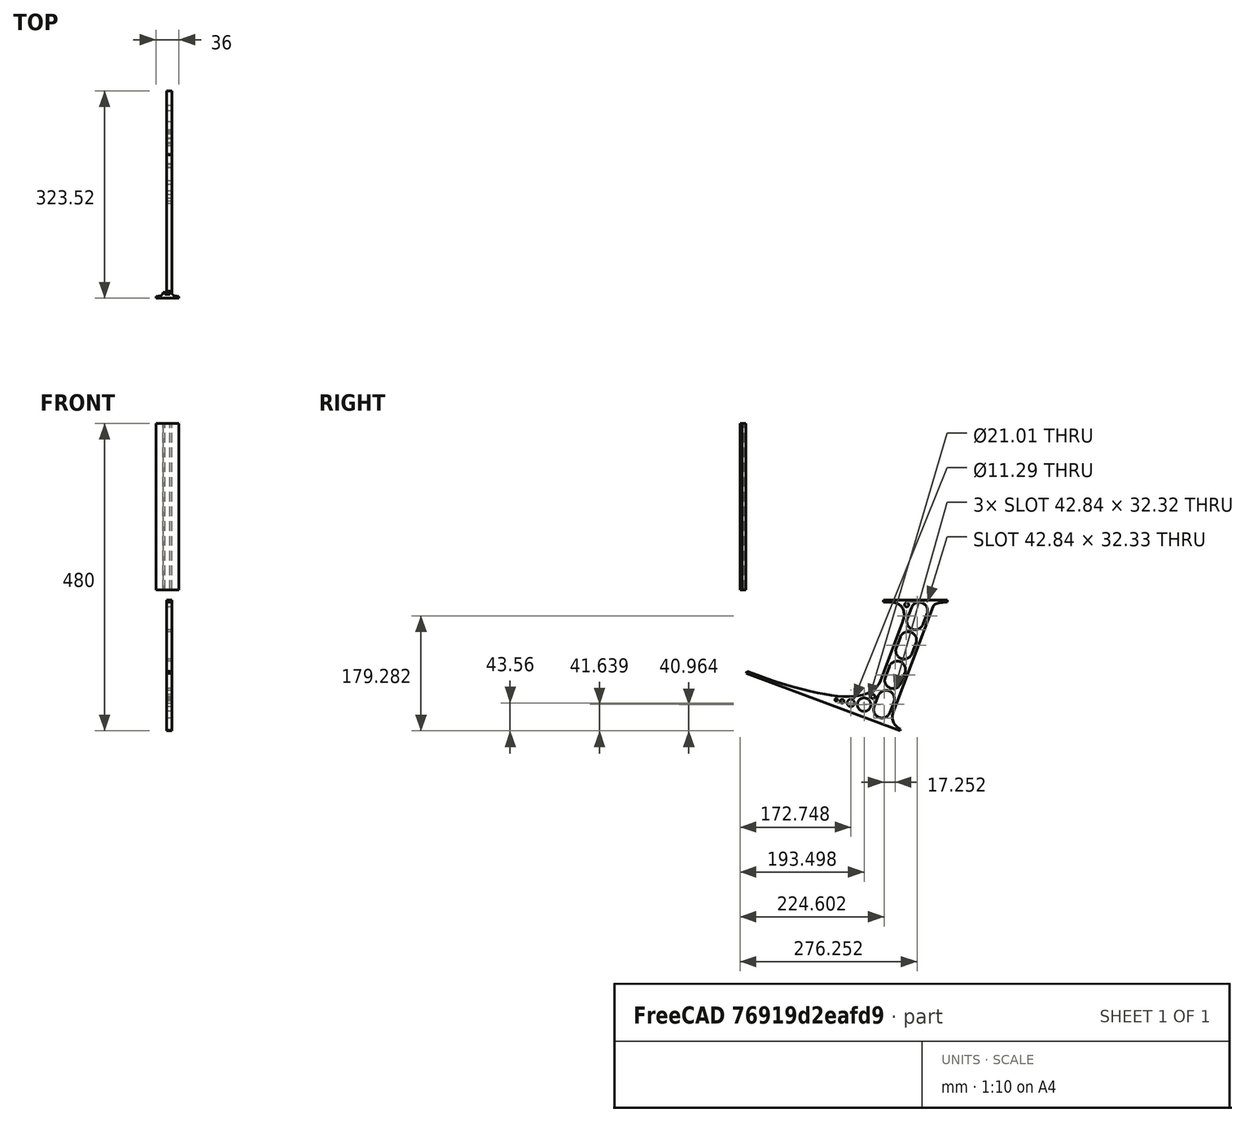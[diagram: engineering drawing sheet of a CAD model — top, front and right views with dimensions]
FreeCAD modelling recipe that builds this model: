
FCSTD DOCUMENT  (FreeCAD 0.19R0.19.2)
Label: laptopStand087
License: All rights reserved
LicenseURL: http://en.wikipedia.org/wiki/All_rights_reserved
objects: Sketcher::SketchObject×3, Part::Extrusion×3
note: 6 computed .brp shape members not serialized (recipe doc carries the construction recipe); baked Part::Feature solids carry a one-line shape summary decoded from their .brp

FEATURE [Sketcher::SketchObject] Sketch
  FullyConstrained = false
  sketch-geometry (236):
    g0: LineSegment StartX=-10.9272 StartY=-82.7794 StartZ=0 EndX=46.0728 EndY=-51.4823 EndZ=0
    g1: LineSegment StartX=366.073 StartY=-91.7794 StartZ=0 EndX=318.073 EndY=-65.424 EndZ=0
    g2: LineSegment StartX=-10.9272 StartY=77.3346 StartZ=0 EndX=-10.9272 EndY=-82.7794 EndZ=0
    g3: LineSegment StartX=375.073 StartY=-82.7794 StartZ=0 EndX=375.073 EndY=83.9235 EndZ=0
    g4: LineSegment StartX=-1.92719 StartY=-91.7794 StartZ=0 EndX=46.0728 EndY=-91.7794 EndZ=0
    g5: LineSegment StartX=318.073 StartY=124.221 StartZ=0 EndX=366.073 EndY=124.221 EndZ=0
    g6: LineSegment StartX=306.073 StartY=77.3346 StartZ=0 EndX=306.073 EndY=-44.8935 EndZ=0
    g7: LineSegment StartX=318.073 StartY=83.9235 StartZ=0 EndX=318.073 EndY=-51.4823 EndZ=0
    g8: LineSegment StartX=318.073 StartY=-51.4823 StartZ=0 EndX=375.073 EndY=-82.7794 EndZ=0
    g9: LineSegment StartX=318.073 StartY=-65.424 StartZ=0 EndX=318.073 EndY=-91.7794 EndZ=0
    g10: LineSegment StartX=318.073 StartY=-91.7794 StartZ=0 EndX=366.073 EndY=-91.7794 EndZ=0
    g11: LineSegment StartX=58.0728 StartY=-44.8935 StartZ=0 EndX=58.0728 EndY=77.3346 EndZ=0
    g12: LineSegment StartX=46.0728 StartY=-65.424 StartZ=0 EndX=-1.92719 EndY=-91.7794 EndZ=0
    g13: LineSegment StartX=46.0728 StartY=-65.424 StartZ=0 EndX=46.0728 EndY=-91.7794 EndZ=0
    g14: LineSegment StartX=46.0728 StartY=77.3346 StartZ=0 EndX=46.0728 EndY=-51.4823 EndZ=0
    g15: LineSegment StartX=-42.9272 StartY=136.221 StartZ=0 EndX=-42.9272 EndY=-103.779 EndZ=0
    g16: LineSegment StartX=407.073 StartY=136.221 StartZ=0 EndX=407.073 EndY=-103.779 EndZ=0
    g17: ArcOfCircle CenterX=-26.9272 CenterY=22.1087 CenterZ=0 NormalX=0 NormalY=0 NormalZ=1 AngleXU=0 Radius=8 StartAngle=1e-16 EndAngle=3.14159
    g18: ArcOfCircle CenterX=-26.9272 CenterY=-83.7794 CenterZ=0 NormalX=0 NormalY=0 NormalZ=1 AngleXU=0 Radius=8 StartAngle=3.14159 EndAngle=6.28319
    g19: LineSegment StartX=-34.9272 StartY=22.1087 StartZ=0 EndX=-34.9272 EndY=-83.7794 EndZ=0
    g20: LineSegment StartX=-18.9272 StartY=22.1087 StartZ=0 EndX=-18.9272 EndY=-83.7794 EndZ=0
    g21: ArcOfCircle CenterX=391.073 CenterY=22.1087 CenterZ=0 NormalX=0 NormalY=0 NormalZ=1 AngleXU=0 Radius=8 StartAngle=-4.4e-15 EndAngle=3.14159
    g22: LineSegment StartX=399.073 StartY=22.1087 StartZ=0 EndX=399.073 EndY=-83.7794 EndZ=0
    g23: LineSegment StartX=383.073 StartY=22.1087 StartZ=0 EndX=383.073 EndY=-83.7794 EndZ=0
    g24: ArcOfCircle CenterX=391.073 CenterY=-83.7794 CenterZ=0 NormalX=0 NormalY=0 NormalZ=1 AngleXU=0 Radius=8 StartAngle=3.14159 EndAngle=6.28319
    g25: Circle CenterX=175.022 CenterY=27.0628 CenterZ=0 NormalX=0 NormalY=0 NormalZ=1 AngleXU=0 Radius=1
    g26: Circle CenterX=179.022 CenterY=24.8665 CenterZ=0 NormalX=0 NormalY=0 NormalZ=1 AngleXU=0 Radius=1
    g27: Circle CenterX=179.022 CenterY=27.0628 CenterZ=0 NormalX=0 NormalY=0 NormalZ=1 AngleXU=0 Radius=1
    g28: BSplineCurve PolesCount=3 KnotsCount=2 Degree=2 IsPeriodic=0
    g29: GeomPoint X=175.022 Y=27.0628 Z=0
    g30: GeomPoint X=179.022 Y=27.0628 Z=0
    g31: Circle CenterX=189.124 CenterY=27.0628 CenterZ=0 NormalX=0 NormalY=0 NormalZ=1 AngleXU=0 Radius=1
    g32: Circle CenterX=185.124 CenterY=24.8665 CenterZ=0 NormalX=0 NormalY=0 NormalZ=1 AngleXU=0 Radius=1
    g33: Circle CenterX=185.124 CenterY=27.0628 CenterZ=0 NormalX=0 NormalY=0 NormalZ=1 AngleXU=0 Radius=1
    g34: BSplineCurve PolesCount=3 KnotsCount=2 Degree=2 IsPeriodic=0
    g35: GeomPoint X=189.124 Y=27.0628 Z=0
    g36: GeomPoint X=185.124 Y=27.0628 Z=0
    g37: Circle CenterX=175.022 CenterY=5.37834 CenterZ=0 NormalX=0 NormalY=0 NormalZ=1 AngleXU=0 Radius=1
    g38: Circle CenterX=179.022 CenterY=7.57463 CenterZ=0 NormalX=0 NormalY=0 NormalZ=1 AngleXU=0 Radius=1
    g39: Circle CenterX=179.022 CenterY=5.34704 CenterZ=0 NormalX=0 NormalY=0 NormalZ=1 AngleXU=0 Radius=1
    g40: BSplineCurve PolesCount=3 KnotsCount=2 Degree=2 IsPeriodic=0
    g41: GeomPoint X=175.022 Y=5.37834 Z=0
    g42: GeomPoint X=179.022 Y=5.34704 Z=0
    g43: Circle CenterX=189.124 CenterY=5.37834 CenterZ=0 NormalX=0 NormalY=0 NormalZ=1 AngleXU=0 Radius=1
    g44: Circle CenterX=185.124 CenterY=7.57463 CenterZ=0 NormalX=0 NormalY=0 NormalZ=1 AngleXU=0 Radius=1
    g45: Circle CenterX=185.124 CenterY=5.34704 CenterZ=0 NormalX=0 NormalY=0 NormalZ=1 AngleXU=0 Radius=1
    g46: BSplineCurve PolesCount=3 KnotsCount=2 Degree=2 IsPeriodic=0
    g47: GeomPoint X=189.124 Y=5.37834 Z=0
    g48: GeomPoint X=185.124 Y=5.34704 Z=0
    g49: Circle CenterX=165.871 CenterY=18.1458 CenterZ=0 NormalX=0 NormalY=0 NormalZ=1 AngleXU=0 Radius=1
    g50: Circle CenterX=169.377 CenterY=16.2206 CenterZ=0 NormalX=0 NormalY=0 NormalZ=1 AngleXU=0 Radius=1
    g51: Circle CenterX=165.871 CenterY=14.2954 CenterZ=0 NormalX=0 NormalY=0 NormalZ=1 AngleXU=0 Radius=1
    g52: BSplineCurve PolesCount=3 KnotsCount=2 Degree=2 IsPeriodic=0
    g53: GeomPoint X=165.871 Y=18.1458 Z=0
    g54: GeomPoint X=165.871 Y=14.2954 Z=0
    g55: Circle CenterX=198.275 CenterY=18.1458 CenterZ=0 NormalX=0 NormalY=0 NormalZ=1 AngleXU=0 Radius=1
    g56: Circle CenterX=194.768 CenterY=16.2206 CenterZ=0 NormalX=0 NormalY=0 NormalZ=1 AngleXU=0 Radius=1
    g57: Circle CenterX=198.275 CenterY=14.2954 CenterZ=0 NormalX=0 NormalY=0 NormalZ=1 AngleXU=0 Radius=1
    g58: BSplineCurve PolesCount=3 KnotsCount=2 Degree=2 IsPeriodic=0
    g59: GeomPoint X=198.275 Y=18.1458 Z=0
    g60: GeomPoint X=198.275 Y=14.2954 Z=0
    g61: LineSegment StartX=165.871 StartY=18.1458 StartZ=0 EndX=58.0728 EndY=77.3346 EndZ=0
    g62: LineSegment StartX=58.0728 StartY=-44.8935 StartZ=0 EndX=165.871 EndY=14.2954 EndZ=0
    g63: LineSegment StartX=198.275 StartY=18.1458 StartZ=0 EndX=306.073 EndY=77.3346 EndZ=0
    g64: LineSegment StartX=198.275 StartY=14.2954 StartZ=0 EndX=306.073 EndY=-44.8935 EndZ=0
    g65: LineSegment StartX=407.073 StartY=-103.779 StartZ=0 EndX=-42.9272 EndY=-103.779 EndZ=0
    g66: LineSegment StartX=407.073 StartY=136.221 StartZ=0 EndX=-42.9272 EndY=136.221 EndZ=0
    g67: LineSegment StartX=46.0728 StartY=77.3346 StartZ=0 EndX=-10.9272 EndY=77.3346 EndZ=0
    g68: LineSegment StartX=46.0728 StartY=105.865 StartZ=0 EndX=31.5028 EndY=105.865 EndZ=0
    g69: LineSegment StartX=46.0728 StartY=124.221 StartZ=0 EndX=46.0728 EndY=105.865 EndZ=0
    g70: LineSegment StartX=-1.92719 StartY=124.221 StartZ=0 EndX=31.5028 EndY=105.865 EndZ=0
    g71: LineSegment StartX=46.0728 StartY=124.221 StartZ=0 EndX=-1.92719 EndY=124.221 EndZ=0
    g72: LineSegment StartX=318.073 StartY=83.9235 StartZ=0 EndX=375.073 EndY=83.9235 EndZ=0
    g73: LineSegment StartX=318.073 StartY=105.865 StartZ=0 EndX=332.643 EndY=105.865 EndZ=0
    g74: LineSegment StartX=332.643 StartY=105.865 StartZ=0 EndX=366.073 EndY=124.221 EndZ=0
    g75: LineSegment StartX=318.073 StartY=124.221 StartZ=0 EndX=318.073 EndY=105.865 EndZ=0
    g76: Circle CenterX=125.607 CenterY=54.1951 CenterZ=0 NormalX=0 NormalY=0 NormalZ=1 AngleXU=0 Radius=1
    g77: Circle CenterX=139.632 CenterY=46.4944 CenterZ=0 NormalX=0 NormalY=0 NormalZ=1 AngleXU=0 Radius=1
    g78: Circle CenterX=127.326 CenterY=56.7187 CenterZ=0 NormalX=0 NormalY=0 NormalZ=1 AngleXU=0 Radius=1
    g79: BSplineCurve PolesCount=3 KnotsCount=2 Degree=2 IsPeriodic=0
    g80: GeomPoint X=125.607 Y=54.1951 Z=0
    g81: GeomPoint X=127.326 Y=56.7187 Z=0
    g82: Circle CenterX=236.821 CenterY=56.7187 CenterZ=0 NormalX=0 NormalY=0 NormalZ=1 AngleXU=0 Radius=1
    g83: Circle CenterX=224.513 CenterY=46.4944 CenterZ=0 NormalX=0 NormalY=0 NormalZ=1 AngleXU=0 Radius=1
    g84: Circle CenterX=238.538 CenterY=54.1951 CenterZ=0 NormalX=0 NormalY=0 NormalZ=1 AngleXU=0 Radius=1
    g85: BSplineCurve PolesCount=3 KnotsCount=2 Degree=2 IsPeriodic=0
    g86: GeomPoint X=236.821 Y=56.7187 Z=0
    g87: GeomPoint X=238.538 Y=54.1951 Z=0
    g88: Circle CenterX=238.538 CenterY=-21.7539 CenterZ=0 NormalX=0 NormalY=0 NormalZ=1 AngleXU=0 Radius=1
    g89: Circle CenterX=224.513 CenterY=-14.0532 CenterZ=0 NormalX=0 NormalY=0 NormalZ=1 AngleXU=0 Radius=1
    g90: Circle CenterX=236.821 CenterY=-24.2775 CenterZ=0 NormalX=0 NormalY=0 NormalZ=1 AngleXU=0 Radius=1
    g91: BSplineCurve PolesCount=3 KnotsCount=2 Degree=2 IsPeriodic=0
    g92: GeomPoint X=238.538 Y=-21.7539 Z=0
    g93: GeomPoint X=236.821 Y=-24.2775 Z=0
    g94: Circle CenterX=125.607 CenterY=-21.7539 CenterZ=0 NormalX=0 NormalY=0 NormalZ=1 AngleXU=0 Radius=1
    g95: Circle CenterX=139.632 CenterY=-14.0532 CenterZ=0 NormalX=0 NormalY=0 NormalZ=1 AngleXU=0 Radius=1
    g96: Circle CenterX=127.325 CenterY=-24.2775 CenterZ=0 NormalX=0 NormalY=0 NormalZ=1 AngleXU=0 Radius=1
    g97: BSplineCurve PolesCount=3 KnotsCount=2 Degree=2 IsPeriodic=0
    g98: GeomPoint X=125.607 Y=-21.7539 Z=0
    g99: GeomPoint X=127.325 Y=-24.2775 Z=0
    g100: Circle CenterX=302.996 CenterY=111.695 CenterZ=0 NormalX=0 NormalY=0 NormalZ=1 AngleXU=0 Radius=1
    g101: Circle CenterX=306.073 CenterY=114.251 CenterZ=0 NormalX=0 NormalY=0 NormalZ=1 AngleXU=0 Radius=1
    g102: Circle CenterX=306.073 CenterY=110.251 CenterZ=0 NormalX=0 NormalY=0 NormalZ=1 AngleXU=0 Radius=1
    g103: BSplineCurve PolesCount=3 KnotsCount=2 Degree=2 IsPeriodic=0
    g104: GeomPoint X=302.996 Y=111.695 Z=0
    g105: GeomPoint X=306.073 Y=110.251 Z=0
    g106: Circle CenterX=306.073 CenterY=95.2763 CenterZ=0 NormalX=0 NormalY=0 NormalZ=1 AngleXU=0 Radius=1
    g107: Circle CenterX=306.073 CenterY=91.2763 CenterZ=0 NormalX=0 NormalY=0 NormalZ=1 AngleXU=0 Radius=1
    g108: Circle CenterX=302.567 CenterY=89.3511 CenterZ=0 NormalX=0 NormalY=0 NormalZ=1 AngleXU=0 Radius=1
    g109: BSplineCurve PolesCount=3 KnotsCount=2 Degree=2 IsPeriodic=0
    g110: GeomPoint X=306.073 Y=95.2763 Z=0
    g111: GeomPoint X=302.567 Y=89.3511 Z=0
    g112: LineSegment StartX=306.073 StartY=110.251 StartZ=0 EndX=306.073 EndY=95.2763 EndZ=0
    g113: LineSegment StartX=302.996 StartY=111.695 StartZ=0 EndX=236.821 EndY=56.7187 EndZ=0
    g114: LineSegment StartX=238.538 StartY=54.1951 StartZ=0 EndX=302.567 EndY=89.3511 EndZ=0
    g115: Circle CenterX=61.1496 CenterY=111.695 CenterZ=0 NormalX=0 NormalY=0 NormalZ=1 AngleXU=0 Radius=1
    g116: Circle CenterX=58.0728 CenterY=114.251 CenterZ=0 NormalX=0 NormalY=0 NormalZ=1 AngleXU=0 Radius=1
    g117: Circle CenterX=58.0728 CenterY=110.251 CenterZ=0 NormalX=0 NormalY=0 NormalZ=1 AngleXU=0 Radius=1
    g118: BSplineCurve PolesCount=3 KnotsCount=2 Degree=2 IsPeriodic=0
    g119: GeomPoint X=61.1496 Y=111.695 Z=0
    g120: GeomPoint X=58.0728 Y=110.251 Z=0
    g121: Circle CenterX=61.5791 CenterY=89.3511 CenterZ=0 NormalX=0 NormalY=0 NormalZ=1 AngleXU=0 Radius=1
    g122: Circle CenterX=58.0728 CenterY=91.2763 CenterZ=0 NormalX=0 NormalY=0 NormalZ=1 AngleXU=0 Radius=1
    g123: Circle CenterX=58.0728 CenterY=95.2763 CenterZ=0 NormalX=0 NormalY=0 NormalZ=1 AngleXU=0 Radius=1
    g124: BSplineCurve PolesCount=3 KnotsCount=2 Degree=2 IsPeriodic=0
    g125: GeomPoint X=61.5791 Y=89.3511 Z=0
    g126: GeomPoint X=58.0728 Y=95.2763 Z=0
    g127: LineSegment StartX=58.0728 StartY=110.251 StartZ=0 EndX=58.0728 EndY=95.2763 EndZ=0
    g128: LineSegment StartX=61.1496 StartY=111.695 StartZ=0 EndX=127.326 EndY=56.7187 EndZ=0
    g129: LineSegment StartX=125.607 StartY=54.1951 StartZ=0 EndX=61.5791 EndY=89.3511 EndZ=0
    g130: Circle CenterX=61.5791 CenterY=-56.9099 CenterZ=0 NormalX=0 NormalY=0 NormalZ=1 AngleXU=0 Radius=1
    g131: Circle CenterX=58.0728 CenterY=-58.8351 CenterZ=0 NormalX=0 NormalY=0 NormalZ=1 AngleXU=0 Radius=1
    g132: Circle CenterX=58.0728 CenterY=-62.8351 CenterZ=0 NormalX=0 NormalY=0 NormalZ=1 AngleXU=0 Radius=1
    g133: BSplineCurve PolesCount=3 KnotsCount=2 Degree=2 IsPeriodic=0
    g134: GeomPoint X=61.5791 Y=-56.9099 Z=0
    g135: GeomPoint X=58.0728 Y=-62.8351 Z=0
    g136: Circle CenterX=58.0728 CenterY=-77.8102 CenterZ=0 NormalX=0 NormalY=0 NormalZ=1 AngleXU=0 Radius=1
    g137: Circle CenterX=58.0728 CenterY=-81.8102 CenterZ=0 NormalX=0 NormalY=0 NormalZ=1 AngleXU=0 Radius=1
    g138: Circle CenterX=61.1496 CenterY=-79.2541 CenterZ=0 NormalX=0 NormalY=0 NormalZ=1 AngleXU=0 Radius=1
    g139: BSplineCurve PolesCount=3 KnotsCount=2 Degree=2 IsPeriodic=0
    g140: GeomPoint X=58.0728 Y=-77.8102 Z=0
    g141: GeomPoint X=61.1496 Y=-79.2541 Z=0
    g142: LineSegment StartX=58.0728 StartY=-62.8351 StartZ=0 EndX=58.0728 EndY=-77.8102 EndZ=0
    g143: LineSegment StartX=61.1496 StartY=-79.2541 StartZ=0 EndX=127.325 EndY=-24.2775 EndZ=0
    g144: LineSegment StartX=125.607 StartY=-21.7539 StartZ=0 EndX=61.5791 EndY=-56.9099 EndZ=0
    g145: Circle CenterX=302.567 CenterY=-56.9099 CenterZ=0 NormalX=0 NormalY=0 NormalZ=1 AngleXU=0 Radius=1
    g146: Circle CenterX=306.073 CenterY=-58.8351 CenterZ=0 NormalX=0 NormalY=0 NormalZ=1 AngleXU=0 Radius=1
    g147: Circle CenterX=306.073 CenterY=-62.8351 CenterZ=0 NormalX=0 NormalY=0 NormalZ=1 AngleXU=0 Radius=1
    g148: BSplineCurve PolesCount=3 KnotsCount=2 Degree=2 IsPeriodic=0
    g149: GeomPoint X=302.567 Y=-56.9099 Z=0
    g150: GeomPoint X=306.073 Y=-62.8351 Z=0
    g151: Circle CenterX=302.996 CenterY=-79.2541 CenterZ=0 NormalX=0 NormalY=0 NormalZ=1 AngleXU=0 Radius=1
    g152: Circle CenterX=306.073 CenterY=-81.8102 CenterZ=0 NormalX=0 NormalY=0 NormalZ=1 AngleXU=0 Radius=1
    g153: Circle CenterX=306.073 CenterY=-77.8102 CenterZ=0 NormalX=0 NormalY=0 NormalZ=1 AngleXU=0 Radius=1
    g154: BSplineCurve PolesCount=3 KnotsCount=2 Degree=2 IsPeriodic=0
    g155: GeomPoint X=302.996 Y=-79.2541 Z=0
    g156: GeomPoint X=306.073 Y=-77.8102 Z=0
    g157: LineSegment StartX=306.073 StartY=-62.8351 StartZ=0 EndX=306.073 EndY=-77.8102 EndZ=0
    g158: LineSegment StartX=302.996 StartY=-79.2541 StartZ=0 EndX=236.821 EndY=-24.2775 EndZ=0
    g159: LineSegment StartX=238.538 StartY=-21.7539 StartZ=0 EndX=302.567 EndY=-56.9099 EndZ=0
    g160: Circle CenterX=61.6457 CenterY=-88.8112 CenterZ=0 NormalX=0 NormalY=0 NormalZ=1 AngleXU=0 Radius=1
    g161: Circle CenterX=58.0728 CenterY=-91.7794 CenterZ=0 NormalX=0 NormalY=0 NormalZ=1 AngleXU=0 Radius=1
    g162: Circle CenterX=63.9135 CenterY=-91.7794 CenterZ=0 NormalX=0 NormalY=0 NormalZ=1 AngleXU=0 Radius=1
    g163: BSplineCurve PolesCount=3 KnotsCount=2 Degree=2 IsPeriodic=0
    g164: GeomPoint X=61.6457 Y=-88.8112 Z=0
    g165: GeomPoint X=63.9135 Y=-91.7794 Z=0
    g166: Circle CenterX=179.022 CenterY=-85.8163 CenterZ=0 NormalX=0 NormalY=0 NormalZ=1 AngleXU=0 Radius=1
    g167: Circle CenterX=179.022 CenterY=-91.7794 CenterZ=0 NormalX=0 NormalY=0 NormalZ=1 AngleXU=0 Radius=1
    g168: Circle CenterX=171.895 CenterY=-91.7794 CenterZ=0 NormalX=0 NormalY=0 NormalZ=1 AngleXU=0 Radius=1
    g169: BSplineCurve PolesCount=3 KnotsCount=2 Degree=2 IsPeriodic=0
    g170: GeomPoint X=179.022 Y=-85.8163 Z=0
    g171: GeomPoint X=171.895 Y=-91.7794 Z=0
    g172: Circle CenterX=185.124 CenterY=-86.2028 CenterZ=0 NormalX=0 NormalY=0 NormalZ=1 AngleXU=0 Radius=1
    g173: Circle CenterX=185.124 CenterY=-91.7794 CenterZ=0 NormalX=0 NormalY=0 NormalZ=1 AngleXU=0 Radius=1
    g174: Circle CenterX=191.747 CenterY=-91.7794 CenterZ=0 NormalX=0 NormalY=0 NormalZ=1 AngleXU=0 Radius=1
    g175: BSplineCurve PolesCount=3 KnotsCount=2 Degree=2 IsPeriodic=0
    g176: GeomPoint X=185.124 Y=-86.2028 Z=0
    g177: GeomPoint X=191.747 Y=-91.7794 Z=0
    g178: Circle CenterX=299.888 CenterY=-86.6413 CenterZ=0 NormalX=0 NormalY=0 NormalZ=1 AngleXU=0 Radius=1
    g179: Circle CenterX=306.073 CenterY=-91.7794 CenterZ=0 NormalX=0 NormalY=0 NormalZ=1 AngleXU=0 Radius=1
    g180: Circle CenterX=298.776 CenterY=-91.7794 CenterZ=0 NormalX=0 NormalY=0 NormalZ=1 AngleXU=0 Radius=1
    g181: BSplineCurve PolesCount=3 KnotsCount=2 Degree=2 IsPeriodic=0
    g182: GeomPoint X=299.888 Y=-86.6413 Z=0
    g183: GeomPoint X=298.776 Y=-91.7794 Z=0
    g184: LineSegment StartX=189.124 StartY=5.37834 StartZ=0 EndX=299.888 EndY=-86.6413 EndZ=0
    g185: LineSegment StartX=298.776 StartY=-91.7794 StartZ=0 EndX=191.747 EndY=-91.7794 EndZ=0
    g186: LineSegment StartX=185.124 StartY=-86.2028 StartZ=0 EndX=185.124 EndY=5.34704 EndZ=0
    g187: LineSegment StartX=179.022 StartY=5.34704 StartZ=0 EndX=179.022 EndY=-85.8163 EndZ=0
    g188: LineSegment StartX=171.895 StartY=-91.7794 StartZ=0 EndX=63.9135 EndY=-91.7794 EndZ=0
    g189: LineSegment StartX=61.6457 StartY=-88.8112 StartZ=0 EndX=175.022 EndY=5.37834 EndZ=0
    g190: Circle CenterX=302.073 CenterY=124.221 CenterZ=0 NormalX=0 NormalY=0 NormalZ=1 AngleXU=0 Radius=1
    g191: Circle CenterX=306.073 CenterY=124.221 CenterZ=0 NormalX=0 NormalY=0 NormalZ=1 AngleXU=0 Radius=1
    g192: Circle CenterX=302.996 CenterY=121.665 CenterZ=0 NormalX=0 NormalY=0 NormalZ=1 AngleXU=0 Radius=1
    g193: BSplineCurve PolesCount=3 KnotsCount=2 Degree=2 IsPeriodic=0
    g194: GeomPoint X=302.073 Y=124.221 Z=0
    g195: GeomPoint X=302.996 Y=121.665 Z=0
    g196: Circle CenterX=189.124 CenterY=124.221 CenterZ=0 NormalX=0 NormalY=0 NormalZ=1 AngleXU=0 Radius=1
    g197: Circle CenterX=185.124 CenterY=124.221 CenterZ=0 NormalX=0 NormalY=0 NormalZ=1 AngleXU=0 Radius=1
    g198: Circle CenterX=185.124 CenterY=120.221 CenterZ=0 NormalX=0 NormalY=0 NormalZ=1 AngleXU=0 Radius=1
    g199: BSplineCurve PolesCount=3 KnotsCount=2 Degree=2 IsPeriodic=0
    g200: GeomPoint X=189.124 Y=124.221 Z=0
    g201: GeomPoint X=185.124 Y=120.221 Z=0
    g202: Circle CenterX=175.022 CenterY=124.221 CenterZ=0 NormalX=0 NormalY=0 NormalZ=1 AngleXU=0 Radius=1
    g203: Circle CenterX=179.022 CenterY=124.221 CenterZ=0 NormalX=0 NormalY=0 NormalZ=1 AngleXU=0 Radius=1
    g204: Circle CenterX=179.022 CenterY=120.221 CenterZ=0 NormalX=0 NormalY=0 NormalZ=1 AngleXU=0 Radius=1
    g205: BSplineCurve PolesCount=3 KnotsCount=2 Degree=2 IsPeriodic=0
    g206: GeomPoint X=175.022 Y=124.221 Z=0
    g207: GeomPoint X=179.022 Y=120.221 Z=0
    g208: Circle CenterX=62.0728 CenterY=124.221 CenterZ=0 NormalX=0 NormalY=0 NormalZ=1 AngleXU=0 Radius=1
    g209: Circle CenterX=58.0728 CenterY=124.221 CenterZ=0 NormalX=0 NormalY=0 NormalZ=1 AngleXU=0 Radius=1
    g210: Circle CenterX=61.1496 CenterY=121.665 CenterZ=0 NormalX=0 NormalY=0 NormalZ=1 AngleXU=0 Radius=1
    g211: BSplineCurve PolesCount=3 KnotsCount=2 Degree=2 IsPeriodic=0
    g212: GeomPoint X=62.0728 Y=124.221 Z=0
    g213: GeomPoint X=61.1496 Y=121.665 Z=0
    g214: LineSegment StartX=62.0728 StartY=124.221 StartZ=0 EndX=175.022 EndY=124.221 EndZ=0
    g215: LineSegment StartX=179.022 StartY=120.221 StartZ=0 EndX=179.022 EndY=27.0628 EndZ=0
    g216: LineSegment StartX=185.124 StartY=27.0628 StartZ=0 EndX=185.124 EndY=120.221 EndZ=0
    g217: LineSegment StartX=189.124 StartY=124.221 StartZ=0 EndX=302.073 EndY=124.221 EndZ=0
    g218: LineSegment StartX=302.996 StartY=121.665 StartZ=0 EndX=189.124 EndY=27.0628 EndZ=0
    g219: LineSegment StartX=175.022 StartY=27.0628 StartZ=0 EndX=61.1496 EndY=121.665 EndZ=0
    g220: LineSegment StartX=58.0728 StartY=77.3346 StartZ=0 EndX=61.5791 EndY=75.4095 EndZ=0
    g221: LineSegment StartX=58.0728 StartY=77.3346 StartZ=0 EndX=58.0728 EndY=73.3346 EndZ=0
    g222: LineSegment StartX=58.0728 StartY=-44.8935 StartZ=0 EndX=58.0728 EndY=-40.8935 EndZ=0
    g223: LineSegment StartX=58.0728 StartY=-44.8935 StartZ=0 EndX=61.5791 EndY=-42.9683 EndZ=0
    g224: Circle CenterX=61.5791 CenterY=75.4095 CenterZ=0 NormalX=0 NormalY=0 NormalZ=1 AngleXU=0 Radius=1
    g225: Circle CenterX=58.0728 CenterY=77.3346 CenterZ=0 NormalX=0 NormalY=0 NormalZ=1 AngleXU=0 Radius=1
    g226: Circle CenterX=58.0728 CenterY=73.3346 CenterZ=0 NormalX=0 NormalY=0 NormalZ=1 AngleXU=0 Radius=1
    g227: BSplineCurve PolesCount=3 KnotsCount=2 Degree=2 IsPeriodic=0
    g228: GeomPoint X=61.5791 Y=75.4095 Z=0
    g229: GeomPoint X=58.0728 Y=73.3346 Z=0
    g230: Circle CenterX=58.0728 CenterY=-40.8935 CenterZ=0 NormalX=0 NormalY=0 NormalZ=1 AngleXU=0 Radius=1
    g231: Circle CenterX=58.0728 CenterY=-44.8935 CenterZ=0 NormalX=0 NormalY=0 NormalZ=1 AngleXU=0 Radius=1
    g232: Circle CenterX=61.5791 CenterY=-42.9683 CenterZ=0 NormalX=0 NormalY=0 NormalZ=1 AngleXU=0 Radius=1
    g233: BSplineCurve PolesCount=3 KnotsCount=2 Degree=2 IsPeriodic=0
    g234: GeomPoint X=58.0728 Y=-40.8935 Z=0
    g235: GeomPoint X=61.5791 Y=-42.9683 Z=0
  constraints (411):
    c: Horizontal(g4)
    c: Horizontal(g5)
    c: Coincident(g7,g8)
    c: Coincident(g9,g1)
    c: Tangent(g7,g9)
    c: Coincident(g13,g12)
    c: Coincident(g0,g14)
    c: Block(g8)
    c: Block(g3)
    c: Block(g1)
    c: Block(g9)
    c: Block(g13)
    c: Block(g12)
    c: Block(g0)
    c: Block(g2)
    c: Block(g6)
    c: Block(g5)
    c: Block(g10)
    c: Block(g4)
    c: Vertical(g15)
    c: Vertical(g16)
    c: Block(g16)
    c: Block(g15)
    c: Tangent(g17,g20) = 1.5708
    c: Tangent(g17,g19) = -1.5708
    c: Tangent(g19,g18) = -1.5708
    c: Tangent(g20,g18) = 1.5708
    c: Vertical(g19)
    c: Equal(g17,g18)
    c: Block(g20)
    c: Block(g19)
    c: Tangent(g21,g22) = 1.5708
    c: Tangent(g22,g24) = 1.5708
    c: Equal(g21,g24)
    c: Coincident(g23,g21)
    c: Coincident(g23,g24)
    c: Block(g22)
    c: Block(g23)
    c: Weight(g25) = 1
    c: Equal(g25,g26)
    c: Equal(g25,g27)
    c: InternalAlignment(g25,g28)
    c: InternalAlignment(g26,g28)
    c: InternalAlignment(g27,g28)
    c: InternalAlignment(g29,g28)
    c: InternalAlignment(g30,g28)
    c: Weight(g31) = 1
    c: Equal(g31,g32)
    c: Equal(g31,g33)
    c: InternalAlignment(g31,g34)
    c: InternalAlignment(g32,g34)
    c: InternalAlignment(g33,g34)
    c: InternalAlignment(g35,g34)
    c: InternalAlignment(g36,g34)
    c: Block(g34)
    c: Block(g28)
    c: Weight(g37) = 1
    c: Equal(g37,g38)
    c: Equal(g37,g39)
    c: InternalAlignment(g37,g40)
    c: InternalAlignment(g38,g40)
    c: InternalAlignment(g39,g40)
    c: InternalAlignment(g41,g40)
    c: InternalAlignment(g42,g40)
    c: Weight(g43) = 1
    c: Equal(g43,g44)
    c: Equal(g43,g45)
    c: InternalAlignment(g43,g46)
    c: InternalAlignment(g44,g46)
    c: InternalAlignment(g45,g46)
    c: InternalAlignment(g47,g46)
    c: InternalAlignment(g48,g46)
    c: Block(g46)
    c: Block(g40)
    c: Weight(g49) = 1
    c: Equal(g49,g50)
    c: Equal(g49,g51)
    c: InternalAlignment(g49,g52)
    c: InternalAlignment(g50,g52)
    c: InternalAlignment(g51,g52)
    c: InternalAlignment(g53,g52)
    c: InternalAlignment(g54,g52)
    c: Weight(g55) = 1
    c: Equal(g55,g56)
    c: Equal(g55,g57)
    c: InternalAlignment(g55,g58)
    c: InternalAlignment(g56,g58)
    c: InternalAlignment(g57,g58)
    c: InternalAlignment(g59,g58)
    c: InternalAlignment(g60,g58)
    c: Block(g52)
    c: Block(g58)
    c: Coincident(g61,g52)
    c: Coincident(g61,g11)
    c: Coincident(g62,g11)
    c: Coincident(g62,g52)
    c: Coincident(g63,g58)
    c: Coincident(g63,g6)
    c: Coincident(g64,g58)
    c: Coincident(g64,g6)
    c: Block(g11)
    c: Coincident(g65,g16)
    c: Coincident(g65,g15)
    c: Horizontal(g65)
    c: Distance(g65) = 450
    c: Coincident(g66,g16)
    c: Coincident(g66,g15)
    c: Horizontal(g66)
    c: Horizontal(g67)
    c: Coincident(g14,g67)
    c: Horizontal(g68)
    c: Vertical(g69)
    c: Block(g69)
    c: Block(g68)
    c: Block(g67)
    c: Distance(g69) = 18.3554
    c: Coincident(g71,g69)
    c: Coincident(g71,g70)
    c: Horizontal(g71)
    c: Block(g71)
    c: Block(g70)
    c: Coincident(g68,g70)
    c: Coincident(g2,g67)
    c: Coincident(g72,g7)
    c: Horizontal(g72)
    c: Horizontal(g73)
    c: Block(g72)
    c: Coincident(g74,g5)
    c: Coincident(g75,g5)
    c: Coincident(g75,g73)
    c: Vertical(g75)
    c: Block(g75)
    c: Coincident(g73,g74)
    c: Block(g74)
    c: Coincident(g3,g72)
    c: Weight(g76) = 1
    c: Equal(g76,g77)
    c: Equal(g76,g78)
    c: InternalAlignment(g76,g79)
    c: InternalAlignment(g77,g79)
    c: InternalAlignment(g78,g79)
    c: InternalAlignment(g80,g79)
    c: InternalAlignment(g81,g79)
    c: Block(g79)
    c: Weight(g82) = 1
    c: Equal(g82,g83)
    c: Equal(g82,g84)
    c: InternalAlignment(g82,g85)
    c: InternalAlignment(g83,g85)
    c: InternalAlignment(g84,g85)
    c: InternalAlignment(g86,g85)
    c: InternalAlignment(g87,g85)
    c: Block(g85)
    c: Weight(g88) = 1
    c: Equal(g88,g89)
    c: Equal(g88,g90)
    c: InternalAlignment(g88,g91)
    c: InternalAlignment(g89,g91)
    c: InternalAlignment(g90,g91)
    c: InternalAlignment(g92,g91)
    c: InternalAlignment(g93,g91)
    c: Block(g91)
    c: Weight(g94) = 1
    c: Equal(g94,g95)
    c: Equal(g94,g96)
    c: InternalAlignment(g94,g97)
    c: InternalAlignment(g95,g97)
    c: InternalAlignment(g96,g97)
    c: InternalAlignment(g98,g97)
    c: InternalAlignment(g99,g97)
    c: Block(g97)
    c: Weight(g100) = 1
    c: Equal(g100,g101)
    c: Equal(g100,g102)
    c: InternalAlignment(g100,g103)
    c: InternalAlignment(g101,g103)
    c: InternalAlignment(g102,g103)
    c: InternalAlignment(g104,g103)
    c: InternalAlignment(g105,g103)
    c: Weight(g106) = 1
    c: Equal(g106,g107)
    c: Equal(g106,g108)
    c: InternalAlignment(g106,g109)
    c: InternalAlignment(g107,g109)
    c: InternalAlignment(g108,g109)
    c: InternalAlignment(g110,g109)
    c: InternalAlignment(g111,g109)
    c: Block(g103)
    c: Block(g109)
    c: Coincident(g112,g103)
    c: Coincident(g112,g109)
    c: Vertical(g112)
    c: Coincident(g113,g103)
    c: Coincident(g113,g85)
    c: Coincident(g114,g85)
    c: Coincident(g114,g109)
    c: Weight(g115) = 1
    c: Equal(g115,g116)
    c: Equal(g115,g117)
    c: InternalAlignment(g115,g118)
    c: InternalAlignment(g116,g118)
    c: InternalAlignment(g117,g118)
    c: InternalAlignment(g119,g118)
    c: InternalAlignment(g120,g118)
    c: Weight(g121) = 1
    c: Equal(g121,g122)
    c: Equal(g121,g123)
    c: InternalAlignment(g121,g124)
    c: InternalAlignment(g122,g124)
    c: InternalAlignment(g123,g124)
    c: InternalAlignment(g125,g124)
    c: InternalAlignment(g126,g124)
    c: Block(g118)
    c: Block(g124)
    c: Coincident(g127,g118)
    c: Coincident(g127,g124)
    c: Vertical(g127)
    c: Coincident(g128,g118)
    c: Coincident(g128,g79)
    c: Coincident(g129,g79)
    c: Coincident(g129,g124)
    c: Weight(g130) = 1
    c: Equal(g130,g131)
    c: Equal(g130,g132)
    c: InternalAlignment(g130,g133)
    c: InternalAlignment(g131,g133)
    c: InternalAlignment(g132,g133)
    c: InternalAlignment(g134,g133)
    c: InternalAlignment(g135,g133)
    c: Weight(g136) = 1
    c: Equal(g136,g137)
    c: Equal(g136,g138)
    c: InternalAlignment(g136,g139)
    c: InternalAlignment(g137,g139)
    c: InternalAlignment(g138,g139)
    c: InternalAlignment(g140,g139)
    c: InternalAlignment(g141,g139)
    c: Block(g133)
    c: Block(g139)
    c: Coincident(g142,g133)
    c: Coincident(g142,g139)
    c: Vertical(g142)
    c: Coincident(g143,g139)
    c: Coincident(g143,g97)
    c: Coincident(g144,g97)
    c: Coincident(g144,g133)
    c: Weight(g145) = 1
    c: Equal(g145,g146)
    c: Equal(g145,g147)
    c: InternalAlignment(g145,g148)
    c: InternalAlignment(g146,g148)
    c: InternalAlignment(g147,g148)
    c: InternalAlignment(g149,g148)
    c: InternalAlignment(g150,g148)
    c: Weight(g151) = 1
    c: Equal(g151,g152)
    c: Equal(g151,g153)
    c: InternalAlignment(g151,g154)
    c: InternalAlignment(g152,g154)
    c: InternalAlignment(g153,g154)
    c: InternalAlignment(g155,g154)
    c: InternalAlignment(g156,g154)
    c: Block(g148)
    c: Block(g154)
    c: Coincident(g157,g148)
    c: Coincident(g157,g154)
    c: Vertical(g157)
    c: Coincident(g158,g154)
    c: Coincident(g158,g91)
    c: Coincident(g159,g91)
    c: Coincident(g159,g148)
    c: Weight(g160) = 1
    c: Equal(g160,g161)
    c: Equal(g160,g162)
    c: InternalAlignment(g160,g163)
    c: InternalAlignment(g161,g163)
    c: InternalAlignment(g162,g163)
    c: InternalAlignment(g164,g163)
    c: InternalAlignment(g165,g163)
    c: Weight(g166) = 1
    c: Equal(g166,g167)
    c: Equal(g166,g168)
    c: InternalAlignment(g166,g169)
    c: InternalAlignment(g167,g169)
    c: InternalAlignment(g168,g169)
    c: InternalAlignment(g170,g169)
    c: InternalAlignment(g171,g169)
    c: Weight(g172) = 1
    c: Equal(g172,g173)
    c: Equal(g172,g174)
    c: InternalAlignment(g172,g175)
    c: InternalAlignment(g173,g175)
    c: InternalAlignment(g174,g175)
    c: InternalAlignment(g176,g175)
    c: InternalAlignment(g177,g175)
    c: Weight(g178) = 1
    c: Equal(g178,g179)
    c: Equal(g178,g180)
    c: InternalAlignment(g178,g181)
    c: InternalAlignment(g179,g181)
    c: InternalAlignment(g180,g181)
    c: InternalAlignment(g182,g181)
    c: InternalAlignment(g183,g181)
    c: Block(g181)
    c: Block(g175)
    c: Block(g169)
    c: Block(g163)
    c: Coincident(g184,g46)
    c: Coincident(g184,g181)
    c: Coincident(g185,g181)
    c: Coincident(g185,g175)
    c: Horizontal(g185)
    c: Coincident(g186,g175)
    c: Coincident(g186,g46)
    c: Vertical(g186)
    c: Coincident(g187,g40)
    c: Coincident(g187,g169)
    c: Vertical(g187)
    c: Coincident(g188,g169)
    c: Coincident(g188,g163)
    c: Horizontal(g188)
    c: Coincident(g189,g163)
    c: Coincident(g189,g40)
    c: Weight(g190) = 1
    c: Equal(g190,g191)
    c: Equal(g190,g192)
    c: InternalAlignment(g190,g193)
    c: InternalAlignment(g191,g193)
    c: InternalAlignment(g192,g193)
    c: InternalAlignment(g194,g193)
    c: InternalAlignment(g195,g193)
    c: Weight(g196) = 1
    c: Equal(g196,g197)
    c: Equal(g196,g198)
    c: InternalAlignment(g196,g199)
    c: InternalAlignment(g197,g199)
    c: InternalAlignment(g198,g199)
    c: InternalAlignment(g200,g199)
    c: InternalAlignment(g201,g199)
    c: Weight(g202) = 1
    c: Equal(g202,g203)
    c: Equal(g202,g204)
    c: InternalAlignment(g202,g205)
    c: InternalAlignment(g203,g205)
    c: InternalAlignment(g204,g205)
    c: InternalAlignment(g206,g205)
    c: InternalAlignment(g207,g205)
    c: Weight(g208) = 1
    c: Equal(g208,g209)
    c: Equal(g208,g210)
    c: InternalAlignment(g208,g211)
    c: InternalAlignment(g209,g211)
    c: InternalAlignment(g210,g211)
    c: InternalAlignment(g212,g211)
    c: InternalAlignment(g213,g211)
    c: Block(g211)
    c: Block(g205)
    c: Block(g199)
    c: Block(g193)
    c: Coincident(g214,g211)
    c: Coincident(g214,g205)
    c: Horizontal(g214)
    c: Coincident(g215,g205)
    c: Coincident(g215,g28)
    c: Vertical(g215)
    c: Coincident(g216,g34)
    c: Coincident(g216,g199)
    c: Vertical(g216)
    c: Coincident(g217,g199)
    c: Coincident(g217,g193)
    c: Horizontal(g217)
    c: Coincident(g218,g193)
    c: Coincident(g218,g34)
    c: Coincident(g219,g28)
    c: Coincident(g219,g211)
    c: Vertical(g221)
    c: Vertical(g222)
    c: Parallel(g62,g223)
    c: Parallel(g220,g61)
    c: Distance(g220) = 4
    c: Distance(g221) = 4
    c: Distance(g222) = 4
    c: Distance(g223) = 4
    c: Coincident(g223,g11)
    c: Coincident(g222,g11)
    c: Coincident(g220,g11)
    c: Coincident(g11,g221)
    c: Coincident(g227,g220)
    c: Weight(g224) = 1
    c: Equal(g224,g225)
    c: Coincident(g225,g11)
    c: Equal(g224,g226)
    c: Coincident(g227,g221)
    c: InternalAlignment(g224,g227)
    c: InternalAlignment(g225,g227)
    c: InternalAlignment(g226,g227)
    c: InternalAlignment(g228,g227)
    c: InternalAlignment(g229,g227)
    c: Coincident(g233,g222)
    c: Weight(g230) = 1
    c: Equal(g230,g231)
    c: Coincident(g231,g11)
    c: Equal(g230,g232)
    c: Coincident(g233,g223)
    c: InternalAlignment(g230,g233)
    c: InternalAlignment(g231,g233)
    c: InternalAlignment(g232,g233)
    c: InternalAlignment(g234,g233)
    c: InternalAlignment(g235,g233)
    c: Block(g233)
    c: Block(g227)
FEATURE [Sketcher::SketchObject] Sketch001
  FullyConstrained = true
  MapMode = 4
  Placement = pos=(0,0,0) rot=(0.57735,0.57735,0.57735;2.0944rad)
  Support = -> [Sketch]
  sketch-geometry (46):
    g0: BSplineCurve PolesCount=3 KnotsCount=2 Degree=2 IsPeriodic=0
    g1: ArcOfCircle CenterX=73.1223 CenterY=-32.291 CenterZ=0 NormalX=0 NormalY=0 NormalZ=1 AngleXU=0 Radius=13 StartAngle=5.92268 EndAngle=9.06428
    g2: ArcOfCircle CenterX=66.7816 CenterY=-49.1439 CenterZ=0 NormalX=0 NormalY=0 NormalZ=1 AngleXU=0 Radius=13 StartAngle=2.78068 EndAngle=5.92131
    g3: ArcOfCircle CenterX=55.9263 CenterY=-78.1807 CenterZ=0 NormalX=0 NormalY=0 NormalZ=1 AngleXU=0 Radius=13 StartAngle=5.92268 EndAngle=9.06428
    g4: ArcOfCircle CenterX=49.5884 CenterY=-95.0342 CenterZ=0 NormalX=0 NormalY=0 NormalZ=1 AngleXU=0 Radius=13 StartAngle=2.78068 EndAngle=5.92131
    g5: ArcOfCircle CenterX=38.7206 CenterY=-124.067 CenterZ=0 NormalX=0 NormalY=0 NormalZ=1 AngleXU=0 Radius=13 StartAngle=5.92268 EndAngle=9.06428
    g6: ArcOfCircle CenterX=32.3875 CenterY=-140.92 CenterZ=0 NormalX=0 NormalY=0 NormalZ=1 AngleXU=0 Radius=13 StartAngle=2.78068 EndAngle=5.92131
    g7: ArcOfCircle CenterX=21.4715 CenterY=-169.934 CenterZ=0 NormalX=0 NormalY=0 NormalZ=1 AngleXU=0 Radius=13 StartAngle=5.92268 EndAngle=9.06428
    g8: ArcOfCircle CenterX=15.1336 CenterY=-186.787 CenterZ=0 NormalX=0 NormalY=0 NormalZ=1 AngleXU=0 Radius=13 StartAngle=2.78068 EndAngle=5.92131
    g9-g12: Circle x4 (B-spline internal-alignment scaffolding for g13; pole/knot coordinates omitted)
    g13: BSplineCurve PolesCount=4 KnotsCount=2 Degree=3 IsPeriodic=0
    g14: GeomPoint X=28.8094 Y=-19.0875 Z=0
    g15: GeomPoint X=47.0443 Y=-50.4712 Z=0
    g16: Circle CenterX=53.5586 CenterY=-23.2695 CenterZ=0 NormalX=0 NormalY=0 NormalZ=1 AngleXU=0 Radius=3.24518
    g17: Circle CenterX=-195.441 CenterY=-127.082 CenterZ=0 NormalX=0 NormalY=0 NormalZ=1 AngleXU=0 Radius=1
    g18: Circle CenterX=-8.24091 CenterY=-197.481 CenterZ=0 NormalX=0 NormalY=0 NormalZ=1 AngleXU=0 Radius=1
    g19: Circle CenterX=12.8789 CenterY=-141.321 CenterZ=0 NormalX=0 NormalY=0 NormalZ=1 AngleXU=0 Radius=1
    g20: BSplineCurve PolesCount=3 KnotsCount=2 Degree=2 IsPeriodic=0
    g21: GeomPoint X=-195.441 Y=-127.082 Z=0
    g22: GeomPoint X=12.8789 Y=-141.321 Z=0
    g23: Circle CenterX=-12.8016 CenterY=-179.036 CenterZ=0 NormalX=0 NormalY=0 NormalZ=1 AngleXU=0 Radius=10.5072
    g24: Circle CenterX=0.933922 CenterY=-166.43 CenterZ=0 NormalX=0 NormalY=0 NormalZ=1 AngleXU=0 Radius=3.26661
    g25: Circle CenterX=-33.5518 CenterY=-176.44 CenterZ=0 NormalX=0 NormalY=0 NormalZ=1 AngleXU=0 Radius=5.64388
    g26: Circle CenterX=-47.2366 CenterY=-173.859 CenterZ=0 NormalX=0 NormalY=0 NormalZ=1 AngleXU=0 Radius=3.01653
    g27: Circle CenterX=-56.2595 CenterY=-171.456 CenterZ=0 NormalX=0 NormalY=0 NormalZ=1 AngleXU=0 Radius=2.12826
    g28: ArcOfCircle CenterX=51.2151 CenterY=-198.473 CenterZ=0 NormalX=0 NormalY=0 NormalZ=1 AngleXU=0 Radius=20 StartAngle=2.78189 EndAngle=4.35269
    g29: LineSegment StartX=32.4951 StartY=-191.433 StartZ=0 EndX=94.6578 EndY=-26.1352 EndZ=0
    g30: LineSegment StartX=43.1192 StartY=-220.001 StartZ=0 EndX=-196.497 EndY=-129.89 EndZ=0
    g31: LineSegment StartX=43.1192 StartY=-220.001 StartZ=0 EndX=44.1752 EndY=-217.193 EndZ=0
    g32: LineSegment StartX=117.223 StartY=-19.0875 StartZ=0 EndX=117.223 EndY=-16.0875 EndZ=0
    g33: LineSegment StartX=117.223 StartY=-16.0875 StartZ=0 EndX=17.2232 EndY=-16.0875 EndZ=0
    g34: LineSegment StartX=17.2232 StartY=-16.0875 StartZ=0 EndX=17.2232 EndY=-19.0875 EndZ=0
    g35: LineSegment StartX=28.8094 StartY=-19.0875 StartZ=0 EndX=17.2232 EndY=-19.0875 EndZ=0
    g36: LineSegment StartX=47.0443 StartY=-50.4712 StartZ=0 EndX=12.8789 EndY=-141.321 EndZ=0
    g37: LineSegment StartX=-195.441 StartY=-127.082 StartZ=0 EndX=-196.497 EndY=-129.89 EndZ=0
    g38: LineSegment StartX=85.2866 StartY=-36.8766 StartZ=0 EndX=78.9396 EndY=-53.7463 EndZ=0
    g39: LineSegment StartX=60.9579 StartY=-27.7053 StartZ=0 EndX=54.6191 EndY=-44.5532 EndZ=0
    g40: LineSegment StartX=68.0907 StartY=-82.7664 StartZ=0 EndX=61.7465 EndY=-99.6365 EndZ=0
    g41: LineSegment StartX=43.7619 StartY=-73.595 StartZ=0 EndX=37.426 EndY=-90.4435 EndZ=0
    g42: LineSegment StartX=50.885 StartY=-128.652 StartZ=0 EndX=44.5456 EndY=-145.522 EndZ=0
    g43: LineSegment StartX=26.5562 StartY=-119.481 StartZ=0 EndX=20.2251 EndY=-136.329 EndZ=0
    g44: LineSegment StartX=9.3071 StartY=-165.349 StartZ=0 EndX=2.97115 EndY=-182.197 EndZ=0
    g45: LineSegment StartX=33.6358 StartY=-174.52 StartZ=0 EndX=27.2917 EndY=-191.39 EndZ=0
  constraints (71):
    c: Block(g0)
    c: Block(g1)
    c: Block(g2)
    c: Block(g4)
    c: Block(g3)
    c: Block(g6)
    c: Block(g5)
    c: Block(g8)
    c: Block(g7)
    c: Weight(g9) = 1
    c: Equal(g9,g10)
    c: Equal(g9,g11)
    c: Equal(g9,g12)
    c: InternalAlignment(g9-g12 -> g13) x4
    c: InternalAlignment(g14,g13)
    c: InternalAlignment(g15,g13)
    c: Block(g16)
    c: Weight(g17) = 1
    c: Equal(g17,g18)
    c: Equal(g17,g19)
    c: InternalAlignment(g17,g20)
    c: InternalAlignment(g18,g20)
    c: InternalAlignment(g19,g20)
    c: InternalAlignment(g21,g20)
    c: InternalAlignment(g22,g20)
    c: Block(g20)
    c: Block(g23)
    c: Block(g24)
    c: Block(g25)
    c: Block(g26)
    c: Block(g27)
    c: Block(g28)
    c: Coincident(g29,g28)
    c: Coincident(g29,g0)
    c: Block(g13)
    c: Coincident(g31,g30)
    c: Coincident(g31,g28)
    c: Block(g31)
    c: Coincident(g32,g0)
    c: Vertical(g32)
    c: Coincident(g33,g32)
    c: Horizontal(g33)
    c: Coincident(g34,g33)
    c: Vertical(g34)
    c: Block(g33)
    c: Coincident(g35,g13)
    c: Coincident(g35,g34)
    c: Horizontal(g35)
    c: Coincident(g36,g13)
    c: Coincident(g36,g20)
    c: Coincident(g37,g20)
    c: Coincident(g37,g30)
    c: Block(g30)
    c: Coincident(g38,g1)
    c: Coincident(g38,g2)
    c: Coincident(g39,g1)
    c: Coincident(g39,g2)
    c: Coincident(g40,g3)
    c: Coincident(g40,g4)
    c: Coincident(g41,g3)
    c: Coincident(g41,g4)
    c: Coincident(g42,g5)
    c: Coincident(g42,g6)
    c: Coincident(g43,g5)
    c: Coincident(g43,g6)
    c: Coincident(g44,g7)
    c: Coincident(g44,g8)
    c: Coincident(g45,g7)
    c: Coincident(g45,g8)
    c: Distance(g30) = 256
    c: Distance(g33) = 100
FEATURE [Part::Extrusion] Extrude002
  Base = -> Sketch001
  Dir = (1,0,0)
  DirMode = 2
  FaceMakerClass = Part::FaceMakerBullseye
  LengthFwd = 8
  LengthRev = 0
  Solid = true
  Symmetric = false
FEATURE [Sketcher::SketchObject] Sketch002
  FullyConstrained = true
  sketch-geometry (20):
    g0: LineSegment StartX=-2.77179 StartY=-200.304 StartZ=0 EndX=5.22821 EndY=-200.304 EndZ=0
    g1: LineSegment StartX=5.22821 StartY=-200.304 StartZ=0 EndX=5.22821 EndY=-197.304 EndZ=0
    g2: LineSegment StartX=-2.77179 StartY=-200.304 StartZ=0 EndX=-2.77179 EndY=-197.304 EndZ=0
    g3: LineSegment StartX=5.22821 StartY=-197.304 StartZ=0 EndX=8.22821 EndY=-197.304 EndZ=0
    g4: LineSegment StartX=-2.77179 StartY=-197.304 StartZ=0 EndX=-5.77179 EndY=-197.304 EndZ=0
    g5: LineSegment StartX=19.2282 StartY=-203.304 StartZ=0 EndX=19.2282 EndY=-206.304 EndZ=0
    g6: LineSegment StartX=-16.7718 StartY=-203.304 StartZ=0 EndX=-16.7718 EndY=-206.304 EndZ=0
    g7: LineSegment StartX=-16.7718 StartY=-206.304 StartZ=0 EndX=19.2282 EndY=-206.304 EndZ=0
    g8: Circle CenterX=-16.7718 CenterY=-203.304 CenterZ=0 NormalX=0 NormalY=0 NormalZ=1 AngleXU=0 Radius=1
    g9: Circle CenterX=-5.77179 CenterY=-203.304 CenterZ=0 NormalX=0 NormalY=0 NormalZ=1 AngleXU=0 Radius=1
    g10: Circle CenterX=-5.77179 CenterY=-197.304 CenterZ=0 NormalX=0 NormalY=0 NormalZ=1 AngleXU=0 Radius=1
    g11: BSplineCurve PolesCount=3 KnotsCount=2 Degree=2 IsPeriodic=0
    g12: GeomPoint X=-16.7718 Y=-203.304 Z=0
    g13: GeomPoint X=-5.77179 Y=-197.304 Z=0
    g14: Circle CenterX=19.2282 CenterY=-203.304 CenterZ=0 NormalX=0 NormalY=0 NormalZ=1 AngleXU=0 Radius=1
    g15: Circle CenterX=8.22821 CenterY=-203.304 CenterZ=0 NormalX=0 NormalY=0 NormalZ=1 AngleXU=0 Radius=1
    g16: Circle CenterX=8.22821 CenterY=-197.304 CenterZ=0 NormalX=0 NormalY=0 NormalZ=1 AngleXU=0 Radius=1
    g17: BSplineCurve PolesCount=3 KnotsCount=2 Degree=2 IsPeriodic=0
    g18: GeomPoint X=19.2282 Y=-203.304 Z=0
    g19: GeomPoint X=8.22821 Y=-197.304 Z=0
  constraints (41):
    c: Horizontal(g0)
    c: Distance(g0) = 8
    c: Coincident(g1,g0)
    c: Vertical(g1)
    c: Distance(g1) = 3
    c: Coincident(g2,g0)
    c: Vertical(g2)
    c: Distance(g2) = 3
    c: Coincident(g3,g1)
    c: Horizontal(g3)
    c: Distance(g3) = 3
    c: Coincident(g4,g2)
    c: Horizontal(g4)
    c: Distance(g4) = 3
    c: Vertical(g5)
    c: Vertical(g6)
    c: Coincident(g7,g6)
    c: Coincident(g7,g5)
    c: Weight(g8) = 1
    c: Equal(g8,g9)
    c: Equal(g8,g10)
    c: Coincident(g11,g4)
    c: InternalAlignment(g8,g11)
    c: InternalAlignment(g9,g11)
    c: InternalAlignment(g10,g11)
    c: InternalAlignment(g12,g11)
    c: InternalAlignment(g13,g11)
    c: Coincident(g17,g5)
    c: Weight(g14) = 1
    c: Equal(g14,g15)
    c: Equal(g14,g16)
    c: Coincident(g17,g3)
    c: InternalAlignment(g14,g17)
    c: InternalAlignment(g15,g17)
    c: InternalAlignment(g16,g17)
    c: InternalAlignment(g18,g17)
    c: InternalAlignment(g19,g17)
    c: Block(g7)
    c: Block(g17)
    c: Block(g11)
    c: Block(g6)
FEATURE [Part::Extrusion] Extrude003
  Base = -> Sketch002
  Dir = (0,0,1)
  DirMode = 2
  FaceMakerClass = Part::FaceMakerBullseye
  LengthFwd = 260
  LengthRev = 0
  Solid = true
  Symmetric = false
FEATURE [Part::Extrusion] Extrude
  Base = -> Sketch
  Dir = (0,0,1)
  DirMode = 2
  FaceMakerClass = Part::FaceMakerBullseye
  LengthFwd = 14
  LengthRev = 0
  Solid = true
  Symmetric = false
